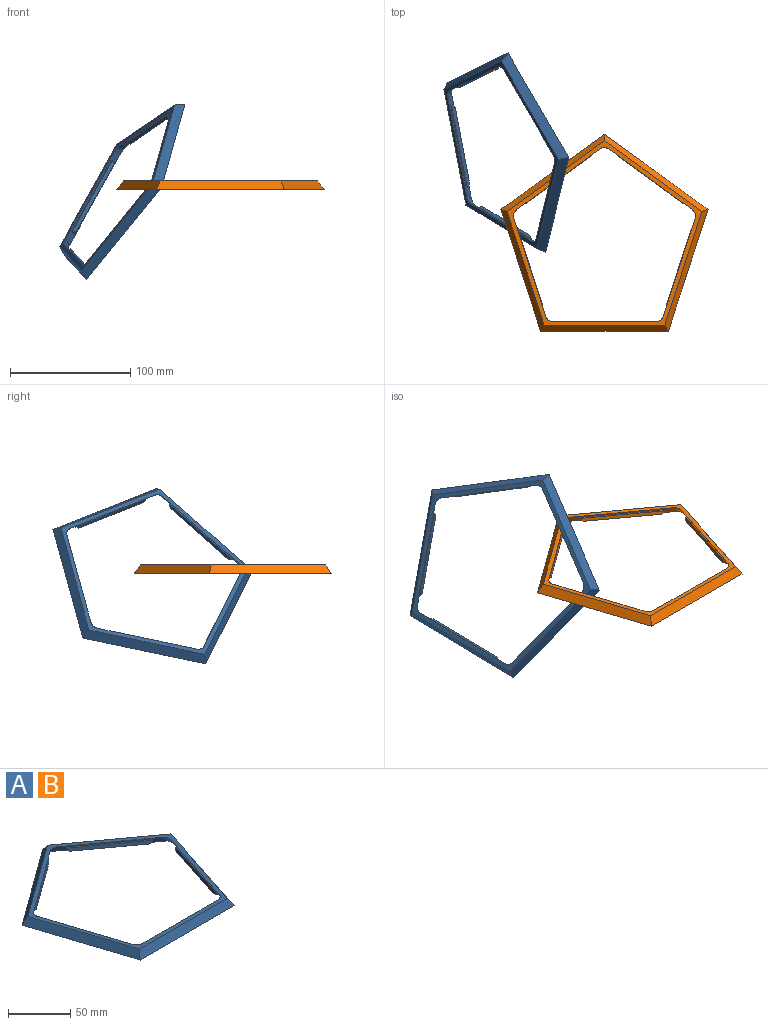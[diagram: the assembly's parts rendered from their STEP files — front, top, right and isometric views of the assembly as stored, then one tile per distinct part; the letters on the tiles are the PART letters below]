
ASSEMBLY  parts=2 mates=1
PART A: 57 faces, bbox 172x163.6x8.3 mm
  f0: plane 171.98x163.56mm, normal (0,0,-1), area 1850.4mm2, adj f2,f3,f4,f5,f6,f7,f8,f9
  f1: plane 161.81x153.9mm, normal (0,0,1), area 1739.6mm2, adj f2,f3,f4,f5,f6,f7,f8,f9
  f2: plane 101.09x35.99mm, normal (0.81,-0.26,0.53), area 848.6mm2, adj f0,f1,f3,f4
  f3: plane 106.29x7mm, normal (0,-0.85,0.53), area 848.6mm2, adj f0,f1,f2,f5
  f4: plane 85.99x64.13mm, normal (0.5,0.69,0.53), area 848.6mm2, adj f0,f1,f2,f6
  f5: plane 101.09x35.99mm, normal (-0.81,-0.26,0.53), area 848.6mm2, adj f0,f1,f3,f6
  f6: plane 85.99x64.13mm, normal (-0.5,0.69,0.53), area 848.6mm2, adj f0,f1,f4,f5
  f7: plane 86.81x31.35mm, normal (-0.81,0.26,-0.53), area 445.1mm2, adj f0,f1,f44,f45,f46,f47,f52,f53
  f8: plane 91.28x7mm, normal (0,0.85,-0.53), area 445.1mm2, adj f0,f1,f12,f13,f14,f15,f52,f54
  f9: plane 73.84x55.3mm, normal (-0.5,-0.69,-0.53), area 445.1mm2, adj f0,f1,f36,f37,f38,f39,f53,f55
  f10: plane 86.81x31.35mm, normal (0.81,0.26,-0.53), area 445.1mm2, adj f0,f1,f20,f21,f22,f23,f54,f56
  f11: plane 73.84x55.3mm, normal (0.5,-0.69,-0.53), area 445.1mm2, adj f0,f1,f28,f29,f30,f31,f55,f56
  f12: plane 3.93x2.95mm, normal (1,0,0), area 4mm2, adj f8,f13,f15,f16
  f13: plane 70x0.85mm, normal (0,-0.53,-0.85), area 70mm2, adj f8,f12,f14,f17
  f14: plane 3.93x2.95mm, normal (-1,0,0), area 4mm2, adj f8,f13,f15,f19
  f15: plane 70x0.85mm, normal (0,0.53,0.85), area 70mm2, adj f8,f12,f14,f18
  f16: plane 3.4x2.75mm, normal (0.71,0.6,-0.37), area 5.7mm2, adj f12,f17,f18
  f17: plane 70x2.75mm, normal (0,0.23,-0.97), area 192.3mm2, adj f13,f16,f18,f19
  f18: plane 70x2.75mm, normal (0,0.97,0.23), area 192.3mm2, adj f15,f16,f17,f19
  f19: plane 3.4x2.75mm, normal (-0.71,0.6,-0.37), area 5.7mm2, adj f14,f17,f18
  f20: plane 3.93x2.81mm, normal (0.31,-0.95,0), area 4mm2, adj f10,f21,f23,f24
  f21: plane 66.84x22.44mm, normal (-0.5,-0.16,-0.85), area 70mm2, adj f10,f20,f22,f25
  f22: plane 3.93x2.81mm, normal (-0.31,0.95,0), area 4mm2, adj f10,f21,f23,f27
  f23: plane 66.84x22.44mm, normal (0.5,0.16,0.85), area 70mm2, adj f10,f20,f22,f26
  f24: plane 3.4x2.75mm, normal (0.79,-0.49,-0.37), area 5.7mm2, adj f20,f25,f26
  f25: plane 66.57x23.63mm, normal (0.22,0.07,-0.97), area 192.3mm2, adj f21,f24,f26,f27
  f26: plane 66.57x21.63mm, normal (0.93,0.3,0.23), area 192.3mm2, adj f23,f24,f25,f27
  f27: plane 3.4x3.24mm, normal (0.35,0.86,-0.37), area 5.7mm2, adj f22,f25,f26
  f28: plane 3.93x2.39mm, normal (-0.81,-0.59,0), area 4mm2, adj f11,f29,f31,f32
  f29: plane 57.13x41.83mm, normal (-0.31,0.43,-0.85), area 70mm2, adj f11,f28,f30,f33
  f30: plane 3.93x2.39mm, normal (0.81,0.59,0), area 4mm2, adj f11,f29,f31,f35
  f31: plane 57.13x41.83mm, normal (0.31,-0.43,0.85), area 70mm2, adj f11,f28,f30,f34
  f32: plane 3.4x3.24mm, normal (-0.22,-0.9,-0.37), area 5.7mm2, adj f28,f33,f34
  f33: plane 56.63x42.2mm, normal (0.14,-0.19,-0.97), area 192.3mm2, adj f29,f32,f34,f35
  f34: plane 56.63x41.15mm, normal (0.57,-0.79,0.23), area 192.3mm2, adj f31,f32,f33,f35
  f35: plane 3.4x3.4mm, normal (0.93,-0.07,-0.37), area 5.7mm2, adj f30,f33,f34
  f36: plane 3.93x2.39mm, normal (-0.81,0.59,0), area 4mm2, adj f9,f37,f39,f40
  f37: plane 57.13x41.83mm, normal (0.31,0.43,-0.85), area 70mm2, adj f9,f36,f38,f41
  f38: plane 3.93x2.39mm, normal (0.81,-0.59,0), area 4mm2, adj f9,f37,f39,f43
  f39: plane 57.13x41.83mm, normal (-0.31,-0.43,0.85), area 70mm2, adj f9,f36,f38,f42
  f40: plane 3.4x3.4mm, normal (-0.93,-0.07,-0.37), area 5.7mm2, adj f36,f41,f42
  f41: plane 56.63x42.2mm, normal (-0.14,-0.19,-0.97), area 192.3mm2, adj f37,f40,f42,f43
  f42: plane 56.63x41.15mm, normal (-0.57,-0.79,0.23), area 192.3mm2, adj f39,f40,f41,f43
  f43: plane 3.4x3.24mm, normal (0.22,-0.9,-0.37), area 5.7mm2, adj f38,f41,f42
  f44: plane 3.93x2.81mm, normal (0.31,0.95,0), area 4mm2, adj f7,f45,f47,f48
  f45: plane 66.84x22.44mm, normal (0.5,-0.16,-0.85), area 70mm2, adj f7,f44,f46,f49
  f46: plane 3.93x2.81mm, normal (-0.31,-0.95,0), area 4mm2, adj f7,f45,f47,f51
  f47: plane 66.84x22.44mm, normal (-0.5,0.16,0.85), area 70mm2, adj f7,f44,f46,f50
  f48: plane 3.4x3.24mm, normal (-0.35,0.86,-0.37), area 5.7mm2, adj f44,f49,f50
  f49: plane 66.57x23.63mm, normal (-0.22,0.07,-0.97), area 192.3mm2, adj f45,f48,f50,f51
  f50: plane 66.57x21.63mm, normal (-0.93,0.3,0.23), area 192.3mm2, adj f47,f48,f49,f51
  f51: plane 3.4x2.75mm, normal (-0.79,-0.49,-0.37), area 5.7mm2, adj f46,f49,f50
  f52: cylinder r=8mm len=9.91mm, axis (0.36,-0.49,-0.79), area 73.8mm2, adj f0,f1,f7,f8
  f53: cylinder r=8mm len=9.42mm, axis (-0.58,-0.19,0.79), area 73.8mm2, adj f0,f1,f7,f9
  f54: cylinder r=8mm len=9.91mm, axis (-0.36,-0.49,-0.79), area 73.8mm2, adj f0,f1,f8,f10
  f55: cylinder r=8mm len=8.3mm, axis (0,-0.61,0.79), area 73.8mm2, adj f0,f1,f9,f11
  f56: cylinder r=8mm len=9.42mm, axis (-0.58,0.19,-0.79), area 73.8mm2, adj f0,f1,f10,f11
PART B: same geometry as A
PLACE A rot(axis=(0.41,-0.89,-0.21),59.8deg) t=(42.31,75.79,-88.45)mm
PLACE B t=(122.43,-1.18,-84.54)mm
MATE parallel B.f5 <-> A.f0  axis (-0.81,-0.26,0.53) through (36.44,26.76,-84.54)mm
